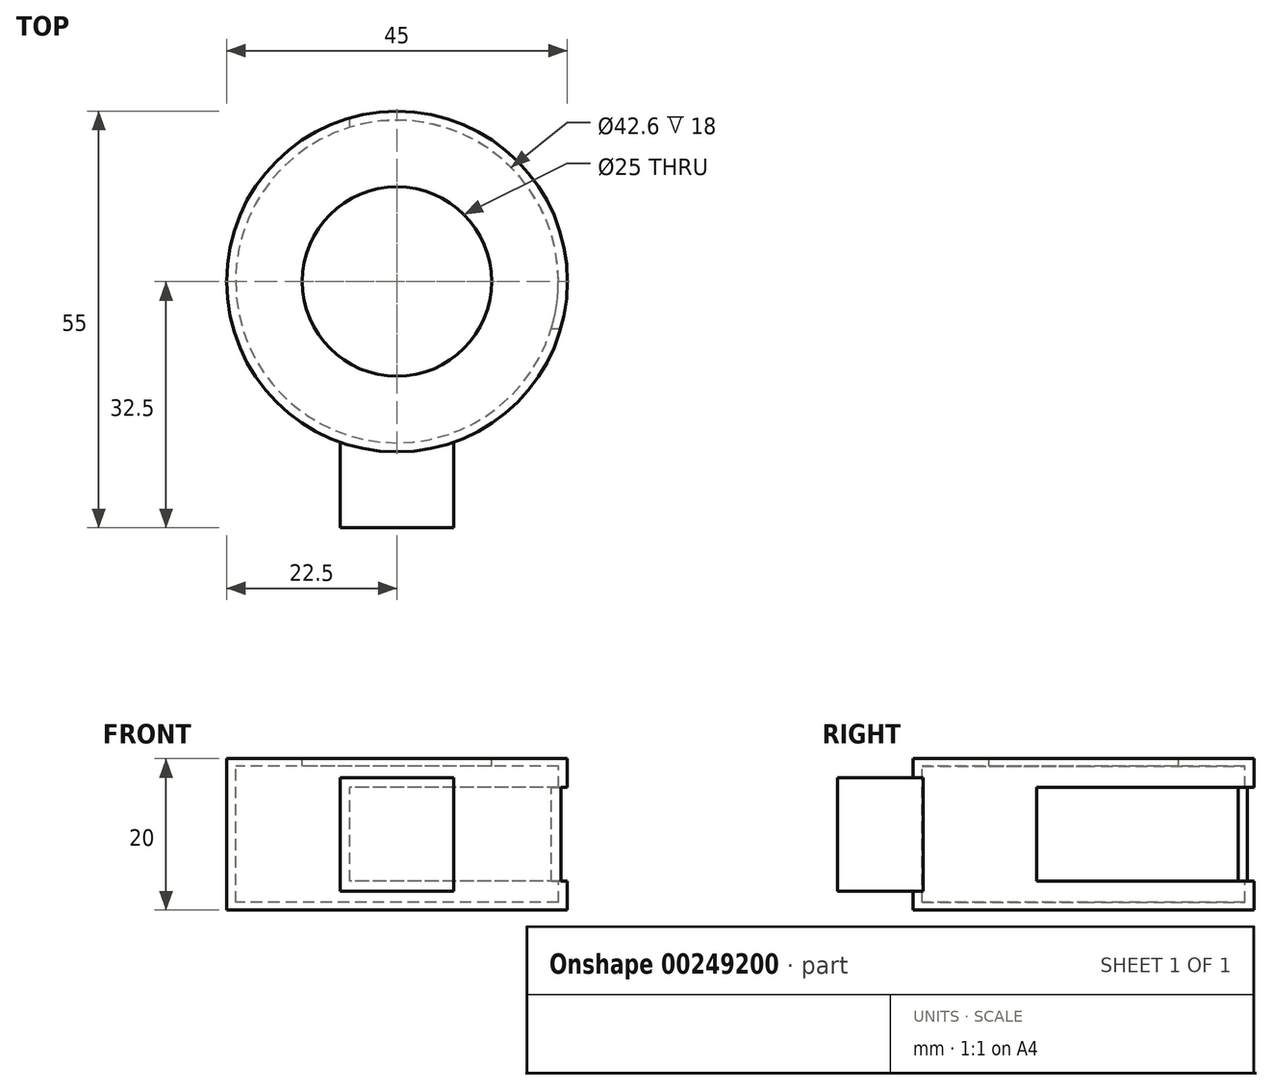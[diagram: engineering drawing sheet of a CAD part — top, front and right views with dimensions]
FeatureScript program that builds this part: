
annotation { "Feature Type Name" : "Feature", "Feature Type Description" : "" }
export const myFeature = defineFeature(function(context is Context, id is Id, definition is map)
    precondition{}
    {
        {
            var Q0;
            Q0=qCreatedBy(makeId("Top.planeOp"),FACE);
            var sketch = newSketch(context, id + "F0", { "sketchPlane" : qUnion([Q0])});
            skCircle(sketch, "E0", {"center": v(0, 0) * mm, "radius": 22.5 * mm});
            skSolve(sketch);
        }
        {
            var Q0;
            Q0 = qSketchRegion(id + "F0", true);
            extrude(context, id + "F1", {"entities" : qUnion([Q0]), "depth" : 10 * mm, "hasSecondDirection" : true, "secondDirectionOppositeDirection" : true, "secondDirectionDepth" : 10 * mm});
        }
        {
            var Q0;
            Q0=qCreatedBy(makeId("Top.planeOp"),FACE);
            var sketch = newSketch(context, id + "F2", { "sketchPlane" : qUnion([Q0])});
            skLineSegment(sketch, "E1.bottom", {"start": v(7.5, -32.5) * mm, "end": v(-7.5, -32.5) * mm});
            skLineSegment(sketch, "E1.top", {"start": v(7.5, -12.5) * mm, "end": v(-7.5, -12.5) * mm});
            skLineSegment(sketch, "E1.left", {"start": v(7.5, -32.5) * mm, "end": v(7.5, -12.5) * mm});
            skLineSegment(sketch, "E1.right", {"start": v(-7.5, -32.5) * mm, "end": v(-7.5, -12.5) * mm});
            skPoint(sketch, "E1.middle", {"position": v(0, -22.5) * mm});
            skSolve(sketch);
        }
        {
            var Q0;
            Q0 = qSketchRegion(id + "F2", true);
            extrude(context, id + "F3", {"entities" : qUnion([Q0]), "operationType" : NewBodyOperationType.ADD, "depth" : 7.5 * mm, "hasSecondDirection" : true, "secondDirectionOppositeDirection" : true, "secondDirectionDepth" : 7.5 * mm});
        }
        {
            var Q0;
            Q0=qCreatedBy(makeId("Top.planeOp"),FACE);
            var sketch = newSketch(context, id + "F4", { "sketchPlane" : qUnion([Q0])});
            skCircle(sketch, "E2", {"center": v(0, 0) * mm, "radius": 21.3 * mm});
            skSolve(sketch);
        }
        {
            var Q0;
            Q0 = qSketchRegion(id + "F4", true);
            extrude(context, id + "F5", {"entities" : qUnion([Q0]), "operationType" : NewBodyOperationType.REMOVE, "oppositeDirection" : true, "depth" : 9 * mm, "hasSecondDirection" : true, "secondDirectionOppositeDirection" : false, "secondDirectionDepth" : 9 * mm});
        }
        {
            var Q0;
            Q0=makeQuery(id+"F1.opExtrude","CAP_FACE",FACE,{"disambiguationData":[OSD([sQuery(id+"F0.wireOp",EDGE,"E0")])],"isStart":false});
            var sketch = newSketch(context, id + "F6", { "sketchPlane" : qUnion([Q0])});
            skCircle(sketch, "E3", {"center": v(0, 0) * mm, "radius": 12.5 * mm});
            skSolve(sketch);
        }
        {
            var Q0;
            Q0 = qSketchRegion(id + "F6", true);
            extrude(context, id + "F7", {"entities" : qUnion([Q0]), "operationType" : NewBodyOperationType.REMOVE, "oppositeDirection" : true, "depth" : 3 * mm});
        }
        {
            var Q0;
            Q0=qCreatedBy(makeId("Top.planeOp"),FACE);
            var sketch = newSketch(context, id + "F8", { "sketchPlane" : qUnion([Q0])});
            skLineSegment(sketch, "E4.bottom", {"start": v(6.2, 6.2) * mm, "end": v(-6.2, 6.2) * mm});
            skLineSegment(sketch, "E4.top", {"start": v(6.2, 31.48) * mm, "end": v(-6.2, 31.48) * mm});
            skLineSegment(sketch, "E4.left", {"start": v(6.2, 6.2) * mm, "end": v(6.2, 31.48) * mm});
            skLineSegment(sketch, "E4.right", {"start": v(-6.2, 6.2) * mm, "end": v(-6.2, 31.48) * mm});
            skPoint(sketch, "E4.middle", {"position": v(0, 18.84) * mm});
            skLineSegment(sketch, "E5.bottom", {"start": v(6.2, 6.2) * mm, "end": v(35, 6.2) * mm});
            skLineSegment(sketch, "E5.top", {"start": v(6.2, -6.2) * mm, "end": v(35, -6.2) * mm});
            skLineSegment(sketch, "E5.left", {"start": v(6.2, 6.2) * mm, "end": v(6.2, -6.2) * mm});
            skLineSegment(sketch, "E5.right", {"start": v(35, 6.2) * mm, "end": v(35, -6.2) * mm});
            skPoint(sketch, "E5.middle", {"position": v(20.6, 0) * mm});
            skLineSegment(sketch, "E6", {"start": v(6.2, 31.48) * mm, "end": v(35, 6.2) * mm});
            skSolve(sketch);
        }
        {
            var Q0;
            Q0 = qSketchRegion(id + "F8", true);
            extrude(context, id + "F9", {"entities" : qUnion([Q0]), "operationType" : NewBodyOperationType.REMOVE, "oppositeDirection" : true, "depth" : 6.2 * mm, "hasSecondDirection" : true, "secondDirectionOppositeDirection" : false, "secondDirectionDepth" : 6.2 * mm});
        }
    });
